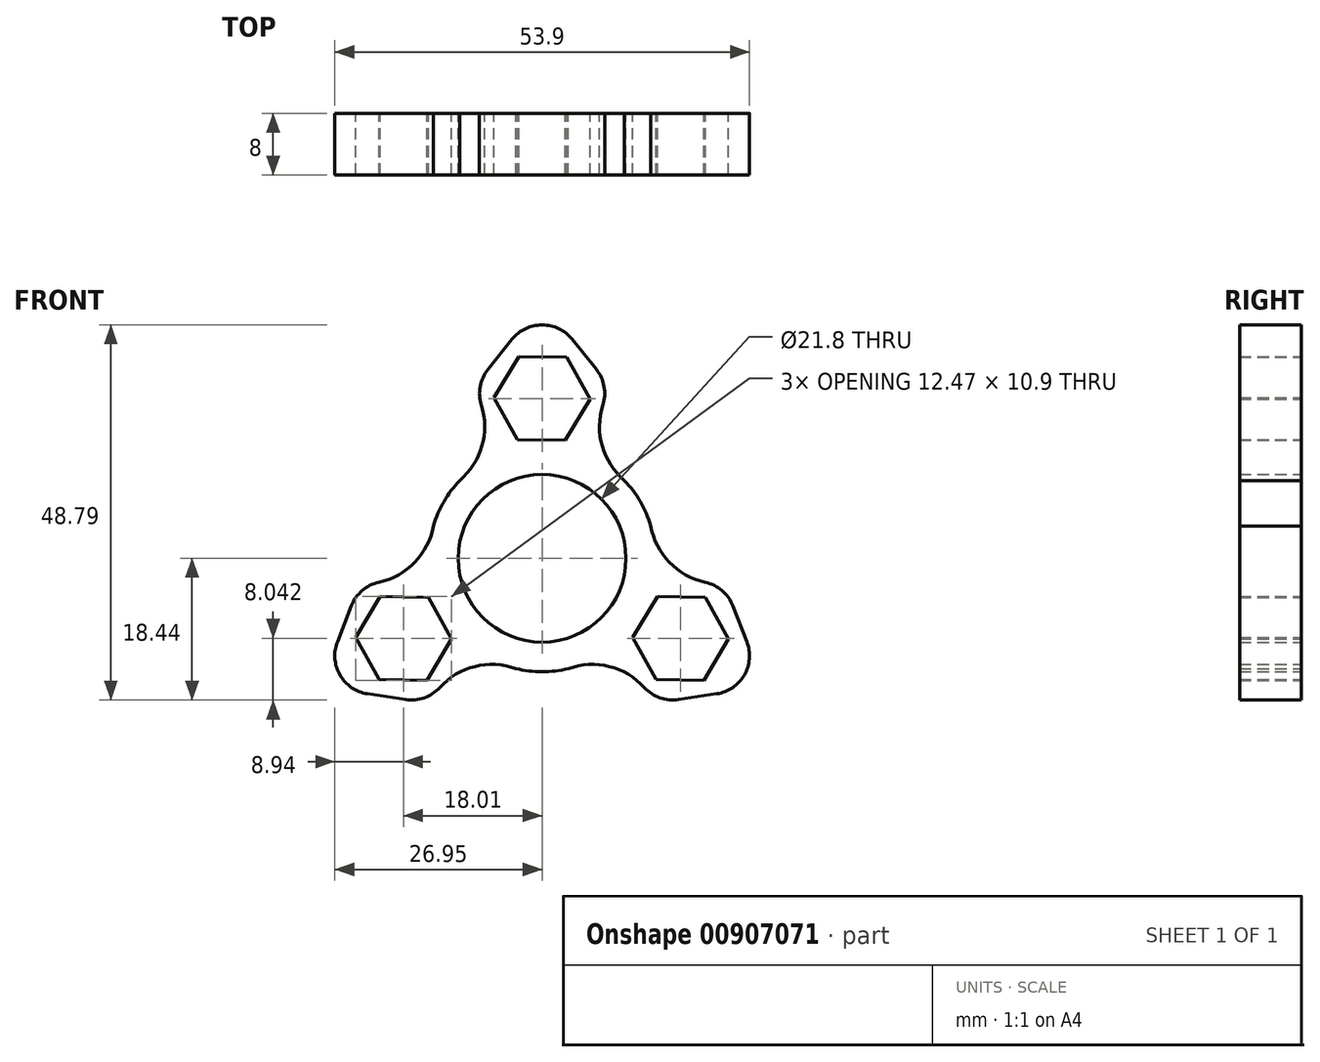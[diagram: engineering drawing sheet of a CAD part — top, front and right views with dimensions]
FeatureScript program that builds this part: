
annotation { "Feature Type Name" : "Feature", "Feature Type Description" : "" }
export const myFeature = defineFeature(function(context is Context, id is Id, definition is map)
    precondition{}
    {
        {
            var Q0;
            Q0=qCreatedBy(makeId("Front.planeOp"),FACE);
            var sketch = newSketch(context, id + "F0", { "sketchPlane" : qUnion([Q0])});
            skPoint(sketch, "E0.end.orphan", {"position": v(7.2, -43.6) * mm});
            skCircle(sketch, "E1", {"center": v(0, 0) * mm, "radius": 10.9 * mm});
            skLineSegment(sketch, "E2", {"start": v(0, 14.75) * mm, "end": v(0, 15.4) * mm});
            skCircle(sketch, "E3", {"center": v(0, 0) * mm, "radius": 14.75 * mm});
            skLineSegment(sketch, "E4", {"start": v(3.9, 28.48) * mm, "end": v(8.97, 22.16) * mm});
            skArc(sketch, "E5", {"start": v(8.97, 22.16) * mm, "mid": v(7.56, 15.8) * mm, "end": v(10.72, 10.13) * mm});
            skLineSegment(sketch, "E6.MirrorCS", {"start": v(-3.9, 28.48) * mm, "end": v(-8.97, 22.16) * mm});
            skArc(sketch, "E7.MirrorCS", {"start": v(-8.97, 22.16) * mm, "mid": v(-7.56, 15.8) * mm, "end": v(-10.72, 10.13) * mm});
            skCircle(sketch, "E8.cCircle", {"center": v(0, 20.8) * mm, "radius": 5.4 * mm, "construction": true});
            skLineSegment(sketch, "E8.0", {"start": v(6.23, 20.7) * mm, "end": v(3.03, 15.35) * mm});
            skLineSegment(sketch, "E8.1", {"start": v(3.03, 15.35) * mm, "end": v(-3.2, 15.45) * mm});
            skLineSegment(sketch, "E8.2", {"start": v(-3.2, 15.45) * mm, "end": v(-6.23, 20.9) * mm});
            skLineSegment(sketch, "E8.3", {"start": v(-6.23, 20.9) * mm, "end": v(-3.03, 26.25) * mm});
            skLineSegment(sketch, "E8.4", {"start": v(-3.03, 26.25) * mm, "end": v(3.2, 26.14) * mm});
            skLineSegment(sketch, "E8.5", {"start": v(3.2, 26.14) * mm, "end": v(6.23, 20.7) * mm});
            skPoint(sketch, "E8.0.midPoint", {"position": v(4.63, 18.02) * mm});
            skLineSegment(sketch, "E9.1.0", {"start": v(-24.24, -10.3) * mm, "end": v(-21.04, -4.95) * mm});
            skLineSegment(sketch, "E9.1.1", {"start": v(-14.98, -15.85) * mm, "end": v(-21.22, -15.75) * mm});
            skLineSegment(sketch, "E9.1.2", {"start": v(-22.71, -17.62) * mm, "end": v(-14.7, -18.85) * mm});
            skLineSegment(sketch, "E9.1.3", {"start": v(-11.78, -10.5) * mm, "end": v(-14.98, -15.85) * mm});
            skLineSegment(sketch, "E9.1.4", {"start": v(-21.04, -4.95) * mm, "end": v(-14.8, -5.05) * mm});
            skLineSegment(sketch, "E9.1.5", {"start": v(-26.61, -10.86) * mm, "end": v(-23.67, -3.3) * mm});
            skLineSegment(sketch, "E9.1.6", {"start": v(-21.22, -15.75) * mm, "end": v(-24.24, -10.3) * mm});
            skPoint(sketch, "E9.1.7", {"position": v(-17.92, -5) * mm});
            skArc(sketch, "E9.1.8", {"start": v(-14.7, -18.85) * mm, "mid": v(-9.91, -14.45) * mm, "end": v(-3.41, -14.35) * mm});
            skArc(sketch, "E9.1.9", {"start": v(-23.67, -3.3) * mm, "mid": v(-17.47, -1.36) * mm, "end": v(-14.13, 4.22) * mm});
            skLineSegment(sketch, "E9.1.11", {"start": v(-14.8, -5.05) * mm, "end": v(-11.78, -10.5) * mm});
            skCircle(sketch, "E9.1.12", {"center": v(-18, -10.4) * mm, "radius": 5.4 * mm, "construction": true});
            skLineSegment(sketch, "E9.2.0", {"start": v(21.04, -15.85) * mm, "end": v(14.8, -15.75) * mm});
            skLineSegment(sketch, "E9.2.1", {"start": v(21.22, -5.05) * mm, "end": v(24.24, -10.5) * mm});
            skLineSegment(sketch, "E9.2.2", {"start": v(26.61, -10.86) * mm, "end": v(23.67, -3.3) * mm});
            skLineSegment(sketch, "E9.2.3", {"start": v(14.98, -4.95) * mm, "end": v(21.22, -5.05) * mm});
            skLineSegment(sketch, "E9.2.4", {"start": v(14.8, -15.75) * mm, "end": v(11.78, -10.3) * mm});
            skLineSegment(sketch, "E9.2.5", {"start": v(22.71, -17.62) * mm, "end": v(14.7, -18.85) * mm});
            skLineSegment(sketch, "E9.2.6", {"start": v(24.24, -10.5) * mm, "end": v(21.04, -15.85) * mm});
            skPoint(sketch, "E9.2.7", {"position": v(13.29, -13.02) * mm});
            skArc(sketch, "E9.2.8", {"start": v(23.67, -3.3) * mm, "mid": v(17.47, -1.36) * mm, "end": v(14.13, 4.22) * mm});
            skArc(sketch, "E9.2.9", {"start": v(14.7, -18.85) * mm, "mid": v(9.91, -14.45) * mm, "end": v(3.41, -14.35) * mm});
            skLineSegment(sketch, "E9.2.11", {"start": v(11.78, -10.3) * mm, "end": v(14.98, -4.95) * mm});
            skCircle(sketch, "E9.2.12", {"center": v(18, -10.4) * mm, "radius": 5.4 * mm, "construction": true});
            skPoint(sketch, "E10.visualSharp", {"position": v(0, 33.34) * mm});
            skArc(sketch, "E10.filletArc", {"start": v(3.9, 28.48) * mm, "mid": v(0, 30.35) * mm, "end": v(-3.9, 28.48) * mm});
            skPoint(sketch, "E11.visualSharp", {"position": v(28.87, -16.67) * mm});
            skArc(sketch, "E11.filletArc", {"start": v(22.71, -17.62) * mm, "mid": v(26.28, -15.18) * mm, "end": v(26.61, -10.86) * mm});
            skPoint(sketch, "E12.visualSharp", {"position": v(-28.87, -16.67) * mm});
            skArc(sketch, "E12.filletArc", {"start": v(-26.61, -10.86) * mm, "mid": v(-26.28, -15.18) * mm, "end": v(-22.71, -17.62) * mm});
            skSolve(sketch);
        }
        {
            var Q0;
            Q0=makeQuery(id+"F0.imprint","IMPRINT",FACE,{"disambiguationData":[TD([[makeQuery(id+"F0.imprint","IMPRINT",EDGE,{"derivedFrom":sQuery(id+"F0.wireOp",EDGE,"E9.1.0")}),1.0]])]});
            var Q1;
            Q1=makeQuery(id+"F0.imprint","IMPRINT",FACE,{"disambiguationData":[TD([[makeQuery(id+"F0.imprint","IMPRINT",EDGE,{"derivedFrom":sQuery(id+"F0.wireOp",EDGE,"E1")}),-1.0]])]});
            var Q2;
            Q2=makeQuery(id+"F0.imprint","IMPRINT",FACE,{"disambiguationData":[TD([[makeQuery(id+"F0.imprint","IMPRINT",EDGE,{"derivedFrom":sQuery(id+"F0.wireOp",EDGE,"E9.2.0")}),1.0]])]});
            var Q3;
            {var subQ8=sQuery(id+"F0.wireOp",EDGE,"E4");Q3=makeQuery(id+"F0.imprint","IMPRINT",FACE,{"disambiguationData":[TD([[makeQuery(id+"F0.imprint","IMPRINT",EDGE,{"derivedFrom":subQ8}),-1.0]])]});}
            extrude(context, id + "F1", {"entities" : qUnion([Q0, Q1, Q2, Q3]), "depth" : 8 * mm, "offsetDistance" : 25 * mm});
        }
        {
            var Q0;
            Q0=makeQuery(id+"F1.opExtrude","SWEPT_EDGE",EDGE,{"disambiguationData":[OSD([sQuery(id+"F0.wireOp",EDGE,"E9.2.2"),sQuery(id+"F0.wireOp",EDGE,"E9.2.5")])]});
            var Q1;
            Q1=makeQuery(id+"F1.opExtrude","SWEPT_EDGE",EDGE,{"disambiguationData":[OSD([sQuery(id+"F0.wireOp",EDGE,"E9.1.2"),sQuery(id+"F0.wireOp",EDGE,"E9.1.5")])]});
            var Q2;
            Q2=makeQuery(id+"F1.opExtrude","SWEPT_EDGE",EDGE,{"disambiguationData":[OSD([sQuery(id+"F0.wireOp",EDGE,"E4"),sQuery(id+"F0.wireOp",EDGE,"E6.MirrorCS")])]});
            fillet(context, id + "F2", {"entities" : qUnion([Q0, Q1, Q2]), "radius" : 5 * mm, "tangentPropagation" : true, "allowEdgeOverflow" : false});
        }
    });
